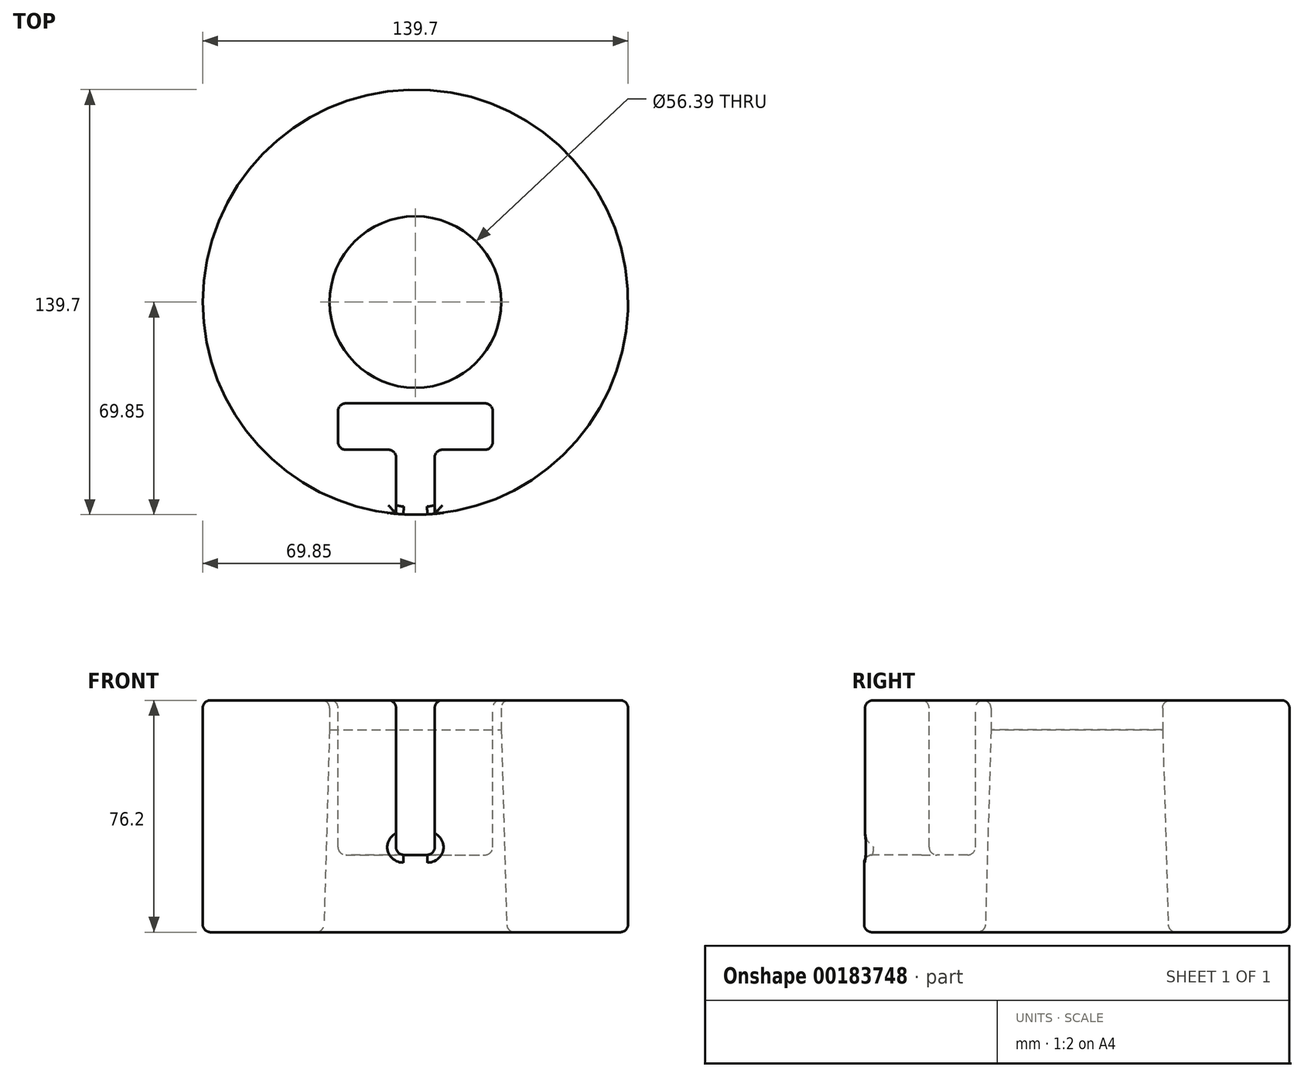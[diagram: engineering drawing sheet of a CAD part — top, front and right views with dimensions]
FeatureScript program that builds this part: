
annotation { "Feature Type Name" : "Feature", "Feature Type Description" : "" }
export const myFeature = defineFeature(function(context is Context, id is Id, definition is map)
    precondition{}
    {
        {
            var Q0;
            Q0=qCreatedBy(makeId("Front.planeOp"),FACE);
            var sketch = newSketch(context, id + "F0", { "sketchPlane" : qUnion([Q0])});
            skLineSegment(sketch, "E0", {"start": v(0, 0) * mm, "end": v(0, 111.83) * mm, "construction": true});
            skLineSegment(sketch, "E1", {"start": v(0, 0) * mm, "end": v(139.72, 0) * mm, "construction": true});
            skLineSegment(sketch, "E2", {"start": v(28.2, 66.55) * mm, "end": v(30.1, 0) * mm});
            skLineSegment(sketch, "E3", {"start": v(30.1, 0) * mm, "end": v(69.85, 0) * mm});
            skLineSegment(sketch, "E4", {"start": v(69.85, 0) * mm, "end": v(69.85, 76.2) * mm});
            skLineSegment(sketch, "E5", {"start": v(69.85, 76.2) * mm, "end": v(28.2, 76.2) * mm});
            skLineSegment(sketch, "E6", {"start": v(28.2, 76.2) * mm, "end": v(28.2, 66.55) * mm});
            skSolve(sketch);
        }
        {
            var Q0;
            Q0 = qSketchRegion(id + "F0", true);
            var Q1;
            Q1=sQuery(id+"F0.wireOp",EDGE,"E0");
            revolve(context, id + "F1", {"entities" : qUnion([Q0]), "axis" : qUnion([Q1]), "revolveType" : RevolveType.FULL});
        }
        {
            var Q0;
            Q0=makeQuery(id+"F1.opRevolve","SWEPT_FACE",FACE,{"disambiguationData":[OSD([sQuery(id+"F0.wireOp",EDGE,"E5")])]});
            var sketch = newSketch(context, id + "F2", { "sketchPlane" : qUnion([Q0])});
            skLineSegment(sketch, "E7", {"start": v(0, 0) * mm, "end": v(0, -33.27) * mm, "construction": true});
            skLineSegment(sketch, "E8", {"start": v(0, 0) * mm, "end": v(69.85, 0) * mm, "construction": true});
            skLineSegment(sketch, "E9.bottom", {"start": v(0, -33.27) * mm, "end": v(25.4, -33.27) * mm});
            skLineSegment(sketch, "E9.top", {"start": v(6.35, -48.51) * mm, "end": v(25.4, -48.51) * mm});
            skLineSegment(sketch, "E9.right", {"start": v(25.4, -33.27) * mm, "end": v(25.4, -48.51) * mm});
            skLineSegment(sketch, "E10.trimOffspring", {"start": v(0, -48.51) * mm, "end": v(0, -69.85) * mm, "construction": true});
            skLineSegment(sketch, "E11.MirrorCS", {"start": v(0, -33.27) * mm, "end": v(-25.4, -33.27) * mm});
            skLineSegment(sketch, "E12.MirrorCS", {"start": v(-25.4, -33.27) * mm, "end": v(-25.4, -48.51) * mm});
            skLineSegment(sketch, "E13.MirrorCS", {"start": v(-6.35, -48.51) * mm, "end": v(-25.4, -48.51) * mm});
            skLineSegment(sketch, "E14", {"start": v(-6.35, -48.51) * mm, "end": v(-6.35, -69.56) * mm});
            skArc(sketch, "E15.0", {"start": v(-6.35, -69.56) * mm, "mid": v(0, -69.85) * mm, "end": v(6.35, -69.56) * mm});
            skLineSegment(sketch, "E16.MirrorCS", {"start": v(6.35, -48.51) * mm, "end": v(6.35, -69.56) * mm});
            skPoint(sketch, "E17.orphan", {"position": v(0, -48.51) * mm});
            skSolve(sketch);
        }
        {
            var Q0;
            Q0 = qSketchRegion(id + "F2", true);
            extrude(context, id + "F3", {"entities" : qUnion([Q0]), "operationType" : NewBodyOperationType.REMOVE, "oppositeDirection" : true, "depth" : 50.8 * mm});
        }
        {
            var Q0;
            Q0=makeQuery(id+"F1.opRevolve","SWEPT_FACE",FACE,{"disambiguationData":[OSD([sQuery(id+"F0.wireOp",EDGE,"E5")])]});
            var Q1;
            Q1=makeQuery(id+"F1.opRevolve","SWEPT_FACE",FACE,{"disambiguationData":[OSD([sQuery(id+"F0.wireOp",EDGE,"E3")])]});
            var Q2;
            Q2=makeQuery(id+"F3.boolean.opBoolean","COPY",FACE,{"derivedFrom":makeQuery(id+"F3.opExtrude","CAP_FACE",FACE,{"disambiguationData":[OSD([sQuery(id+"F2.wireOp",EDGE,"E9.bottom"),sQuery(id+"F2.wireOp",EDGE,"E9.top"),sQuery(id+"F2.wireOp",EDGE,"E9.right"),sQuery(id+"F2.wireOp",EDGE,"E11.MirrorCS"),sQuery(id+"F2.wireOp",EDGE,"E12.MirrorCS"),sQuery(id+"F2.wireOp",EDGE,"E13.MirrorCS"),sQuery(id+"F2.wireOp",EDGE,"E14"),sQuery(id+"F2.wireOp",EDGE,"E15.0"),sQuery(id+"F2.wireOp",EDGE,"E16.MirrorCS")])],"isStart":false})});
            var Q3;
            Q3=makeQuery(id+"F3.boolean.opBoolean","COPY",FACE,{"derivedFrom":makeQuery(id+"F3.opExtrude","SWEPT_FACE",FACE,{"disambiguationData":[OSD([sQuery(id+"F2.wireOp",EDGE,"E12.MirrorCS")])]})});
            var Q4;
            Q4=makeQuery(id+"F3.boolean.opBoolean","COPY",FACE,{"derivedFrom":makeQuery(id+"F3.opExtrude","SWEPT_FACE",FACE,{"disambiguationData":[OSD([sQuery(id+"F2.wireOp",EDGE,"E9.right")])]})});
            var Q5;
            Q5=makeQuery(id+"F3.boolean.opBoolean","COPY",FACE,{"derivedFrom":makeQuery(id+"F3.opExtrude","SWEPT_FACE",FACE,{"disambiguationData":[OSD([sQuery(id+"F2.wireOp",EDGE,"E13.MirrorCS")])]})});
            var Q6;
            Q6=makeQuery(id+"F3.boolean.opBoolean","COPY",FACE,{"derivedFrom":makeQuery(id+"F3.opExtrude","SWEPT_FACE",FACE,{"disambiguationData":[OSD([sQuery(id+"F2.wireOp",EDGE,"E9.top")])]})});
            fillet(context, id + "F4", {"entities" : qUnion([Q0, Q1, Q2, Q3, Q4, Q5, Q6]), "radius" : 2.54 * mm, "tangentPropagation" : true, "allowEdgeOverflow" : false});
        }
    });
